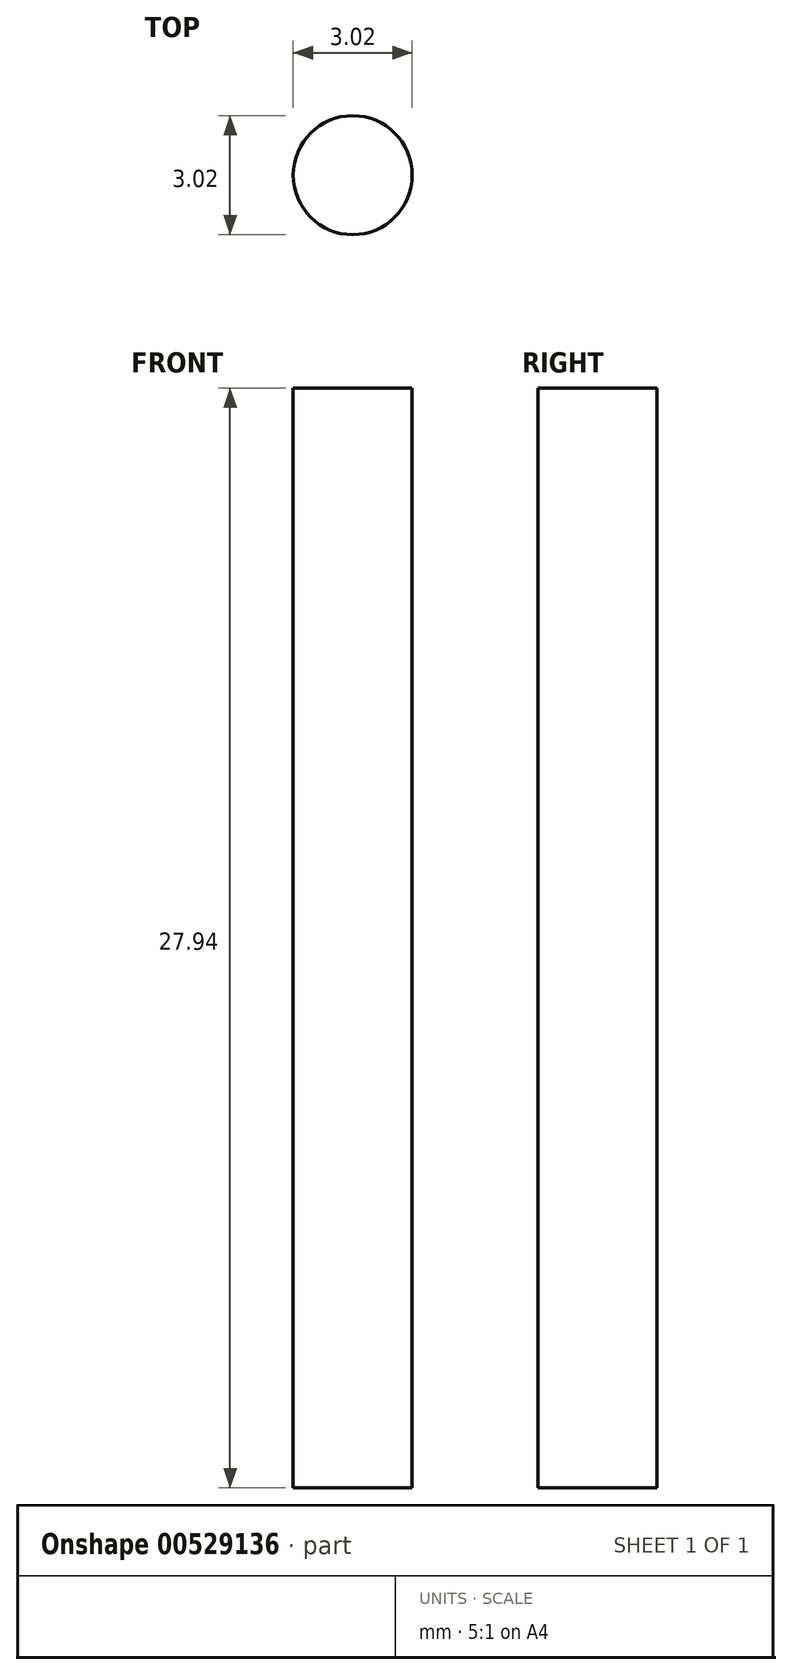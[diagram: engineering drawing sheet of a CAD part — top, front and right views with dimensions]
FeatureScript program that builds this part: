
annotation { "Feature Type Name" : "Feature", "Feature Type Description" : "" }
export const myFeature = defineFeature(function(context is Context, id is Id, definition is map)
    precondition{}
    {
        {
            var Q0;
            Q0=qCreatedBy(makeId("Top.planeOp"),FACE);
            var sketch = newSketch(context, id + "F0", { "sketchPlane" : qUnion([Q0])});
            skCircle(sketch, "E0", {"center": v(0, 0) * mm, "radius": 1.51 * mm});
            skSolve(sketch);
        }
        {
            var Q0;
            Q0 = qSketchRegion(id + "F0", true);
            extrude(context, id + "F1", {"entities" : qUnion([Q0]), "depth" : 27.94 * mm, "offsetDistance" : 25.4 * mm});
        }
    });
